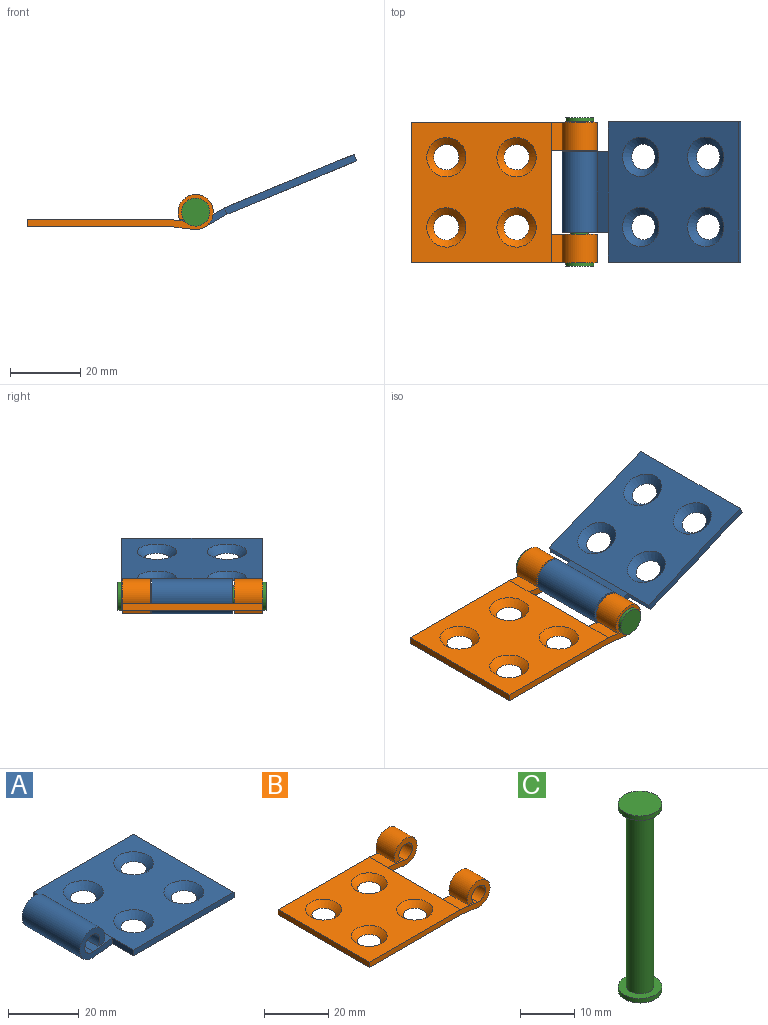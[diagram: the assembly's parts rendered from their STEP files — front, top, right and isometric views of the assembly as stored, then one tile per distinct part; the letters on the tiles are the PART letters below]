
ASSEMBLY  parts=3 mates=2
PART A: 18 faces, bbox 53x40x10 mm
  f0: plane 23x7.35mm, normal (0.13,0,-0.99), area 170.6mm2, adj f1,f12,f14,f16
  f1: cylinder r=5mm len=23mm, axis (0,-1,0), area 604.1mm2, adj f0,f2,f14,f16
  f2: plane 23x2.35mm, normal (0,0,-1), area 54mm2, adj f1,f3,f14,f16
  f3: cylinder r=3mm len=23mm, axis (0,-1,0), area 384.3mm2, adj f2,f4,f14,f16
  f4: plane 23x7.62mm, normal (-0.13,0,0.99), area 176.7mm2, adj f3,f10,f14,f16
  f5: plane 40x2mm, normal (0,1,0), area 80mm2, adj f10,f11,f12,f17
  f6: plane 40x2mm, normal (0,-1,0), area 80mm2, adj f10,f11,f12,f15
  f7: cone r=2.75mm half-angle=45deg, axis (0,0,1), area 81.7mm2, adj f10,f12
  f8: cone r=2.75mm half-angle=45deg, axis (0,0,1), area 81.7mm2, adj f10,f12
  f9: cone r=2.75mm half-angle=45deg, axis (0,0,1), area 81.7mm2, adj f10,f12
  f10: plane 40x40mm, normal (0,0,1), area 1205.9mm2, adj f4,f5,f6,f7,f8,f9,f11,f13
  f11: plane 40x2mm, normal (1,0,0), area 80mm2, adj f5,f6,f10,f12
  f12: plane 40x40mm, normal (0,0,-1), area 1437.1mm2, adj f0,f5,f6,f7,f8,f9,f11,f13
  f13: cone r=2.75mm half-angle=45deg, axis (0,0,1), area 81.7mm2, adj f10,f12
  f14: plane 13x10mm, normal (0,-1,0), area 58mm2, adj f0,f1,f2,f3,f4,f15
  f15: plane 8.5x2mm, normal (-1,0,0), area 17mm2, adj f6,f10,f12,f14
  f16: plane 13x10mm, normal (0,1,0), area 58mm2, adj f0,f1,f2,f3,f4,f17
  f17: plane 8.5x2mm, normal (-1,0,0), area 17mm2, adj f5,f10,f12,f16
PART B: 22 faces, bbox 53x40x10 mm
  f0: plane 8x7.35mm, normal (-0.13,0,-0.99), area 59.3mm2, adj f1,f10,f17,f21
  f1: cylinder r=5mm len=10mm, axis (0,1,0), area 210.1mm2, adj f0,f2,f17,f21
  f2: plane 8x2.35mm, normal (0,0,-1), area 18.8mm2, adj f1,f3,f17,f21
  f3: cylinder r=3mm len=8mm, axis (0,1,0), area 133.7mm2, adj f2,f4,f17,f21
  f4: plane 8x7.62mm, normal (0.13,0,0.99), area 61.4mm2, adj f3,f8,f17,f21
  f5: cone r=2.75mm half-angle=45deg, axis (0,0,1), area 81.7mm2, adj f8,f10
  f6: cone r=2.75mm half-angle=45deg, axis (0,0,1), area 81.7mm2, adj f8,f10
  f7: cone r=2.75mm half-angle=45deg, axis (0,0,1), area 81.7mm2, adj f8,f10
  f8: plane 40x40mm, normal (0,0,1), area 1205.9mm2, adj f4,f5,f6,f7,f9,f15,f16,f17
  f9: plane 40x2mm, normal (-1,0,0), area 80mm2, adj f8,f10,f16,f17
  f10: plane 40x40mm, normal (0,0,-1), area 1437.1mm2, adj f0,f5,f6,f7,f9,f11,f16,f17
  f11: plane 8x7.35mm, normal (-0.13,0,-0.99), area 59.3mm2, adj f10,f12,f16,f20
  f12: cylinder r=5mm len=10mm, axis (0,1,0), area 210.1mm2, adj f11,f13,f16,f20
  f13: plane 8x2.35mm, normal (0,0,-1), area 18.8mm2, adj f12,f14,f16,f20
  f14: cylinder r=3mm len=8mm, axis (0,1,0), area 133.7mm2, adj f13,f15,f16,f20
  f15: plane 8x7.62mm, normal (0.13,0,0.99), area 61.4mm2, adj f8,f14,f16,f20
  f16: plane 53x10mm, normal (0,-1,0), area 138mm2, adj f8,f9,f10,f11,f12,f13,f14,f15
  f17: plane 53x10mm, normal (0,1,0), area 138mm2, adj f0,f1,f2,f3,f4,f8,f9,f10
  f18: cone r=2.75mm half-angle=45deg, axis (0,0,1), area 81.7mm2, adj f8,f10
  f19: plane 24x2mm, normal (1,0,0), area 48mm2, adj f8,f10,f20,f21
  f20: plane 13x10mm, normal (0,1,0), area 58mm2, adj f11,f12,f13,f14,f15,f19
  f21: plane 13x10mm, normal (0,-1,0), area 58mm2, adj f0,f1,f2,f3,f4,f19
PART C: 7 faces, bbox 8x8x42.2 mm
  f0: plane 8x8mm, normal (0,0,1), area 50.3mm2, adj f6
  f1: plane 8x8mm, normal (0,0,-1), area 50.3mm2, adj f2
  f2: cylinder r=4mm len=8mm, axis (0,0,1), area 25.1mm2, adj f1,f3
  f3: plane 8x8mm, normal (0,0,1), area 30.6mm2, adj f2,f4
  f4: cylinder r=2.5mm len=40.2mm, axis (0,0,1), area 631.5mm2, adj f3,f5
  f5: plane 8x8mm, normal (0,0,-1), area 30.6mm2, adj f4,f6
  f6: cylinder r=4mm len=8mm, axis (0,0,1), area 25.1mm2, adj f0,f5
PLACE A rot(axis=(0,-1,0),22.4deg) t=(-2.1,0.2,18.61)mm
PLACE B t=(-96,40.1,0)mm fixed
PLACE C rot(axis=(1,0,0),90deg) t=(-48,-0.9,4)mm
MATE revolute A.f1 <-> C.f2  axis (0,-1,0) through (-48,20.2,4)mm
MATE fastened C.f2 <-> B.f1  axis (0,-1,0) through (-48,0.1,4)mm
